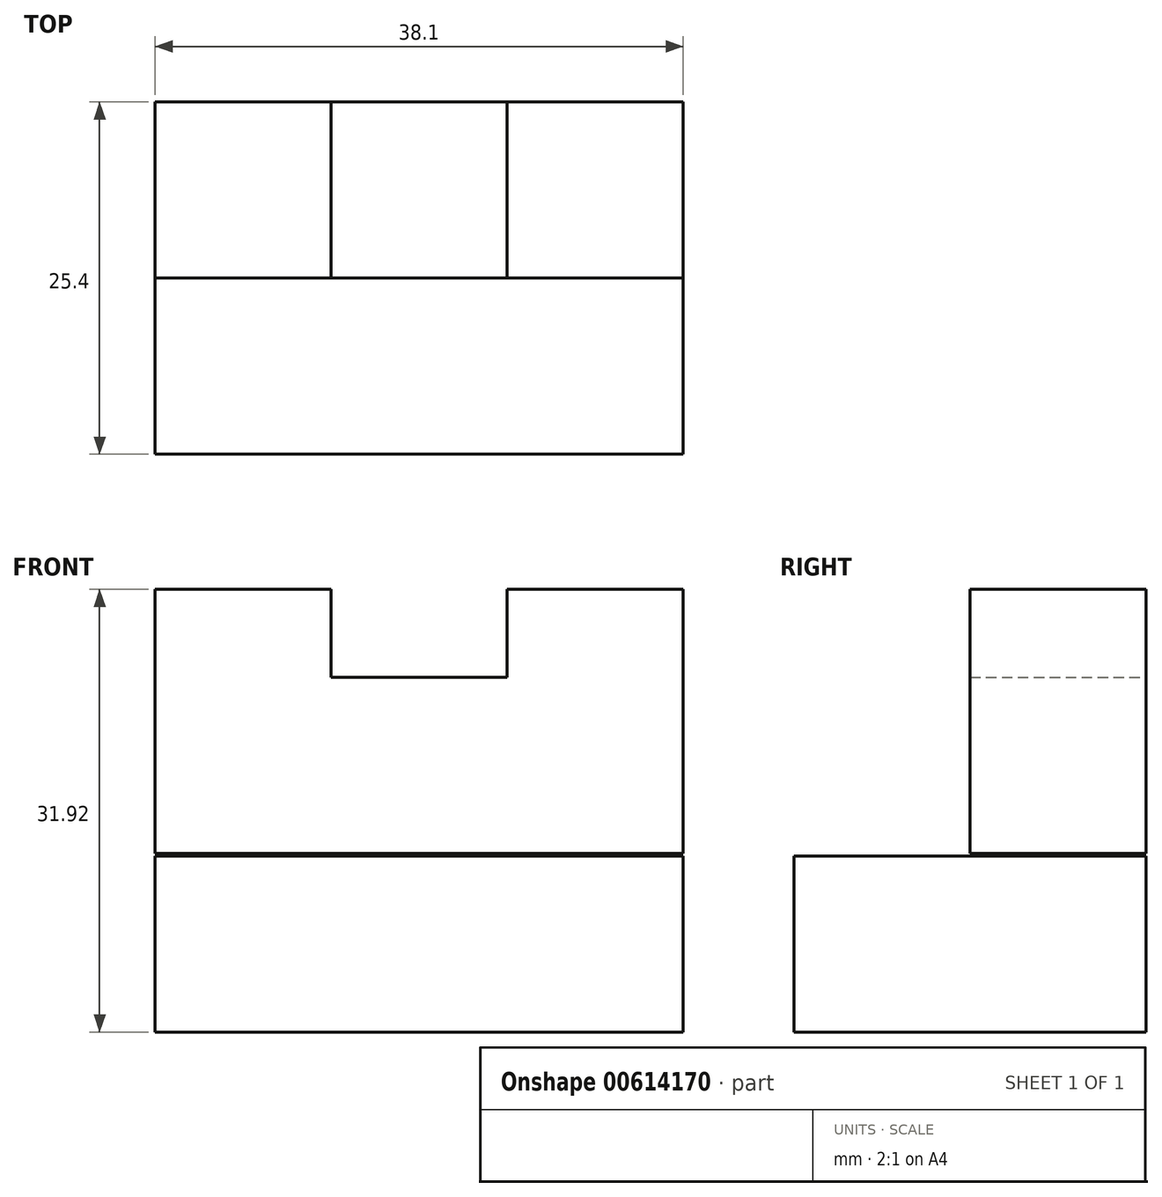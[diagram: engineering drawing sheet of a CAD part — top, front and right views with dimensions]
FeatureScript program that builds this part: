
annotation { "Feature Type Name" : "Feature", "Feature Type Description" : "" }
export const myFeature = defineFeature(function(context is Context, id is Id, definition is map)
    precondition{}
    {
        {
            var Q0;
            Q0=qCreatedBy(makeId("Front.planeOp"),FACE);
            var sketch = newSketch(context, id + "F0", { "sketchPlane" : qUnion([Q0])});
            skLineSegment(sketch, "E0", {"start": v(0, 0) * mm, "end": v(0, 12.7) * mm});
            skLineSegment(sketch, "E1", {"start": v(0, 12.7) * mm, "end": v(38.1, 12.7) * mm});
            skLineSegment(sketch, "E2", {"start": v(38.1, 12.7) * mm, "end": v(38.1, 0) * mm});
            skLineSegment(sketch, "E3", {"start": v(38.1, 0) * mm, "end": v(0, 0) * mm});
            skSolve(sketch);
        }
        {
            var Q0;
            Q0=makeQuery(id+"F0.imprint","IMPRINT",FACE,{"disambiguationData":[TD([[makeQuery(id+"F0.imprint","IMPRINT",EDGE,{"derivedFrom":sQuery(id+"F0.wireOp",EDGE,"E0")}),-1.0]])]});
            extrude(context, id + "F1", {"entities" : qUnion([Q0]), "depth" : 25.4 * mm, "offsetDistance" : 25.4 * mm});
        }
        {
            var Q0;
            Q0=qCreatedBy(makeId("Front.planeOp"),FACE);
            var sketch = newSketch(context, id + "F2", { "sketchPlane" : qUnion([Q0])});
            skLineSegment(sketch, "E4", {"start": v(0, 12.87) * mm, "end": v(0, 31.92) * mm});
            skLineSegment(sketch, "E5", {"start": v(0, 31.92) * mm, "end": v(12.7, 31.92) * mm});
            skLineSegment(sketch, "E6", {"start": v(12.7, 31.92) * mm, "end": v(12.7, 25.57) * mm});
            skLineSegment(sketch, "E7", {"start": v(12.7, 25.57) * mm, "end": v(25.4, 25.57) * mm});
            skLineSegment(sketch, "E8", {"start": v(25.4, 25.57) * mm, "end": v(25.4, 31.92) * mm});
            skLineSegment(sketch, "E9", {"start": v(25.4, 31.92) * mm, "end": v(38.1, 31.92) * mm});
            skLineSegment(sketch, "E10", {"start": v(38.1, 31.92) * mm, "end": v(38.1, 12.87) * mm});
            skLineSegment(sketch, "E11", {"start": v(0, 12.87) * mm, "end": v(38.1, 12.87) * mm});
            skSolve(sketch);
        }
        {
            var Q0;
            Q0=makeQuery(id+"F2.imprint","IMPRINT",FACE,{"disambiguationData":[TD([[makeQuery(id+"F2.imprint","IMPRINT",EDGE,{"derivedFrom":sQuery(id+"F2.wireOp",EDGE,"E4")}),-1.0]])]});
            extrude(context, id + "F3", {"entities" : qUnion([Q0]), "depth" : 12.7 * mm, "offsetDistance" : 25.4 * mm});
        }
    });
